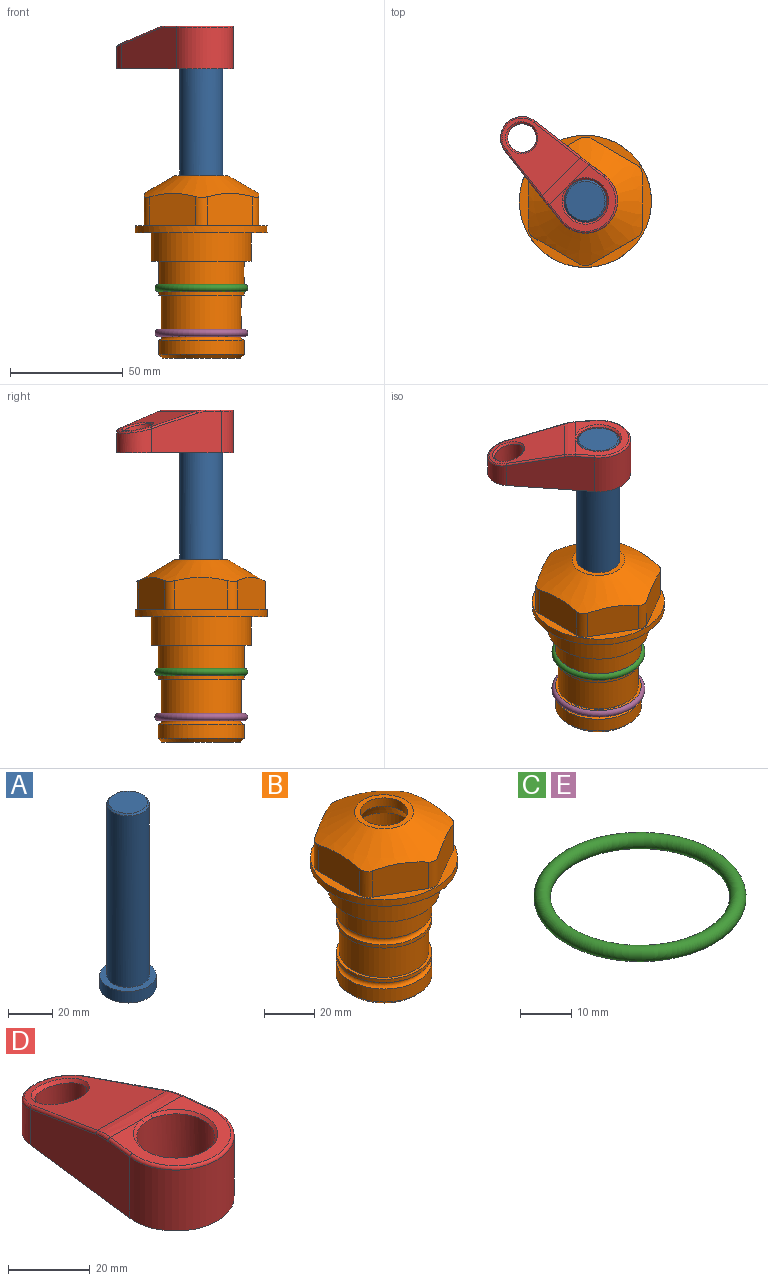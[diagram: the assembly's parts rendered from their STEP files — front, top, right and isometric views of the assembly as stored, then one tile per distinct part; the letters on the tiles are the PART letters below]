
ASSEMBLY  parts=5 mates=3
PART A: 6 faces, bbox 25.4x25.4x101.6 mm
  f0: plane 17.46x17.46mm, normal (0,0,1), area 239.5mm2, adj f5
  f1: plane 25.4x25.4mm, normal (0,0,-1), area 506.7mm2, adj f2
  f2: cylinder r=12.7mm len=25.4mm, axis (0,0,1), area 506.7mm2, adj f1,f3
  f3: plane 25.4x25.4mm, normal (0,0,1), area 221.7mm2, adj f2,f4
  f4: cylinder r=9.53mm len=94.46mm, axis (0,0,1), area 5653mm2, adj f3,f5
  f5: cone r=8.73mm half-angle=45deg, axis (0,0,-1), area 64.4mm2, adj f0,f4
PART B: 36 faces, bbox 58.7x58.7x81 mm
  f0: cylinder r=17.78mm len=35.56mm, axis (0,0,1), area 1670.8mm2, adj f23,f24,f31
  f1: cylinder r=19.05mm len=38.1mm, axis (0,0,1), area 1191.9mm2, adj f26,f27,f30
  f2: plane 58.66x58.66mm, normal (0,0,-1), area 1150.6mm2, adj f3,f28
  f3: cylinder r=29.33mm len=58.66mm, axis (0,0,-1), area 585.1mm2, adj f2,f4
  f4: plane 58.66x58.66mm, normal (0,0,1), area 475.9mm2, adj f3,f5,f6,f7,f8,f9,f10,f11
  f5: plane 20.32x14.34mm, normal (-0.5,0.87,0), area 324.4mm2, adj f4,f15,f16,f17
  f6: plane 20.32x14.34mm, normal (0.5,0.87,0), area 324.4mm2, adj f4,f14,f15,f17
  f7: plane 23.48x14.34mm, normal (1,0,0), area 324.4mm2, adj f4,f13,f14,f17
  f8: plane 20.32x14.34mm, normal (0.5,-0.87,0), area 324.4mm2, adj f4,f12,f13,f17
  f9: plane 20.32x14.34mm, normal (-0.5,-0.87,0), area 324.4mm2, adj f4,f11,f12,f17
  f10: plane 23.48x14.34mm, normal (-1,0,0), area 324.4mm2, adj f4,f11,f16,f17
  f11: cylinder r=5.08mm len=12.85mm, axis (0,0,-1), area 67.2mm2, adj f4,f9,f10,f17
  f12: cylinder r=5.08mm len=12.85mm, axis (0,0,-1), area 67.2mm2, adj f4,f8,f9,f17
  f13: cylinder r=5.08mm len=12.85mm, axis (0,0,-1), area 67.2mm2, adj f4,f7,f8,f17
  f14: cylinder r=5.08mm len=12.85mm, axis (0,0,-1), area 67.2mm2, adj f4,f6,f7,f17
  f15: cylinder r=5.08mm len=12.85mm, axis (0,0,-1), area 67.2mm2, adj f4,f5,f6,f17
  f16: cylinder r=5.08mm len=12.85mm, axis (0,0,-1), area 67.2mm2, adj f4,f5,f10,f17
  f17: cone r=11.73mm half-angle=60deg, axis (0,0,-1), area 2071.8mm2, adj f5,f6,f7,f8,f9,f10,f11,f12
  f18: plane 23.46x23.46mm, normal (0,0,1), area 147.4mm2, adj f17,f35
  f19: plane 34.93x34.93mm, normal (0,0,-1), area 958mm2, adj f29
  f20: cylinder r=19.05mm len=38.1mm, axis (0,0,1), area 760.1mm2, adj f21,f29
  f21: torus R=19.05mm, axis (0,0,1), area 565.3mm2, adj f20,f22
  f22: cylinder r=19.05mm len=38.1mm, axis (0,0,1), area 190mm2, adj f21,f23
  f23: plane 38.1x38.1mm, normal (0,0,1), area 146.9mm2, adj f0,f22
  f24: plane 38.1x38.1mm, normal (0,0,-1), area 146.9mm2, adj f0,f25
  f25: cylinder r=19.05mm len=38.1mm, axis (0,0,1), area 190mm2, adj f24,f26
  f26: torus R=19.05mm, axis (0,0,1), area 565.3mm2, adj f1,f25
  f27: plane 44.45x44.45mm, normal (0,0,-1), area 411.7mm2, adj f1,f28
  f28: cylinder r=22.23mm len=44.45mm, axis (0,0,1), area 1773.5mm2, adj f2,f27
  f29: cone r=19.05mm half-angle=45deg, axis (0,0,1), area 257.5mm2, adj f19,f20
  f30: cylinder r=3.17mm len=6.75mm, axis (-1,0,0), area 128mm2, adj f1,f33
  f31: cylinder r=3.17mm len=6.35mm, axis (-1,0,0), area 102.5mm2, adj f0,f33
  f32: plane 25.4x25.4mm, normal (0,0,1), area 506.7mm2, adj f33
  f33: cylinder r=12.7mm len=66.42mm, axis (0,0,-1), area 5236.2mm2, adj f30,f31,f32,f34
  f34: cone r=9.53mm half-angle=30deg, axis (0,0,-1), area 443.4mm2, adj f33,f35
  f35: cylinder r=9.53mm len=19.05mm, axis (0,0,-1), area 240.9mm2, adj f18,f34
PART C: 1 faces, bbox 44.7x44.7x3.2 mm
  f0: torus R=19.05mm, axis (0,0,1), area 1193.9mm2
PART D: 31 faces, bbox 31.7x65.5x19.8 mm
  f0: plane 39.12x18.26mm, normal (0.99,0.12,0), area 612.2mm2, adj f1,f4,f7,f11,f13,f15
  f1: cylinder r=9.53mm len=18.91mm, axis (0,0,-1), area 296.1mm2, adj f0,f2,f7,f17
  f2: plane 39.12x18.26mm, normal (-0.99,0.12,0), area 612.2mm2, adj f1,f4,f7,f12,f14,f16
  f3: cylinder r=6.35mm len=12.7mm, axis (0,0,-1), area 362.4mm2, adj f7,f18
  f4: cylinder r=14.29mm len=28.58mm, axis (0,0,-1), area 882.2mm2, adj f0,f2,f7,f10
  f5: cylinder r=9.53mm len=19.05mm, axis (0,0,-1), area 1092.6mm2, adj f7,f19,f20
  f6: plane 26.99x23.69mm, normal (0,0,1), area 216.2mm2, adj f9,f10,f11,f12,f19
  f7: plane 63.5x28.58mm, normal (0,0,-1), area 661.8mm2, adj f0,f1,f2,f3,f4,f5,f22,f23
  f8: plane 33.52x23.6mm, normal (0,0.26,0.97), area 486mm2, adj f9,f15,f16,f17,f18
  f9: cylinder r=19.05mm len=24.72mm, axis (1,0,0), area 120.4mm2, adj f6,f8,f13,f14,f20
  f10: torus R=13.49mm, axis (0,0,1), area 59mm2, adj f4,f6,f11,f12
  f11: cylinder r=0.79mm len=8.67mm, axis (0.12,-0.99,0), area 10.8mm2, adj f0,f6,f10,f13
  f12: cylinder r=0.79mm len=8.67mm, axis (0.12,0.99,0), area 10.8mm2, adj f2,f6,f10,f14
  f13: bspline ~4.95x1.42mm, area 6.1mm2, adj f0,f9,f11,f15
  f14: bspline ~4.95x1.42mm, area 6.1mm2, adj f2,f9,f12,f16
  f15: cylinder r=0.79mm len=25.95mm, axis (0.12,-0.96,0.26), area 32.9mm2, adj f0,f8,f13,f17
  f16: cylinder r=0.79mm len=25.95mm, axis (0.12,0.96,-0.26), area 32.9mm2, adj f2,f8,f14,f17
  f17: bspline ~18.91x8.38mm, area 30mm2, adj f1,f8,f15,f16
  f18: bspline ~14.29x14.29mm, area 48.3mm2, adj f3,f8
  f19: cone r=9.53mm half-angle=45deg, axis (0,0,1), area 66.5mm2, adj f5,f6,f20
  f20: bspline ~3.22x0.96mm, area 3.5mm2, adj f5,f9,f19
  f21: plane 2.75x2.72mm, normal (0,0,-1), area 2.9mm2, adj f23,f25,f28
  f22: plane 23.05x15.88mm, normal (-0.99,-0.12,0), area 323.6mm2, adj f7,f25,f26,f27,f28,f29
  f23: plane 23.05x15.88mm, normal (0.99,-0.12,0), area 323.6mm2, adj f7,f21,f25,f27,f28,f30
  f24: cylinder r=9.53mm len=10.69mm, axis (0,0,-1), area 114.7mm2, adj f7,f27,f29,f30
  f25: cylinder r=12.7mm len=20.59mm, axis (0,0,-1), area 381.1mm2, adj f7,f21,f22,f23,f26,f28
  f26: plane 2.75x2.72mm, normal (0,0,-1), area 2.9mm2, adj f22,f25,f28
  f27: plane 19.72x18.37mm, normal (0,-0.26,-0.97), area 291.8mm2, adj f22,f23,f24,f28,f29,f30
  f28: cylinder r=15.88mm len=19.92mm, axis (1,0,0), area 54.8mm2, adj f21,f22,f23,f25,f26,f27
  f29: cylinder r=1.59mm len=11mm, axis (0,0,-1), area 34.7mm2, adj f7,f22,f24,f27
  f30: cylinder r=1.59mm len=11mm, axis (0,0,-1), area 34.7mm2, adj f7,f23,f24,f27
PART E: same geometry as C
PLACE A rot(axis=(0,0,1),45.2deg) t=(0,0,27.55)mm
PLACE B at identity fixed
PLACE C at identity
PLACE D rot(axis=(0,0,1),45.2deg) t=(0,0,28.35)mm
PLACE E t=(0,0,-20)mm
MATE fastened E.f0 <-> B.f0  axis (0,0,1) through (0,0,-44.51)mm
MATE fastened A.f2 <-> D.f4  axis (0,0,1) through (0,0,91.05)mm
MATE cylindrical B.f0 <-> A.f2  axis (0,0,-1) through (0,0,-50.55)mm
